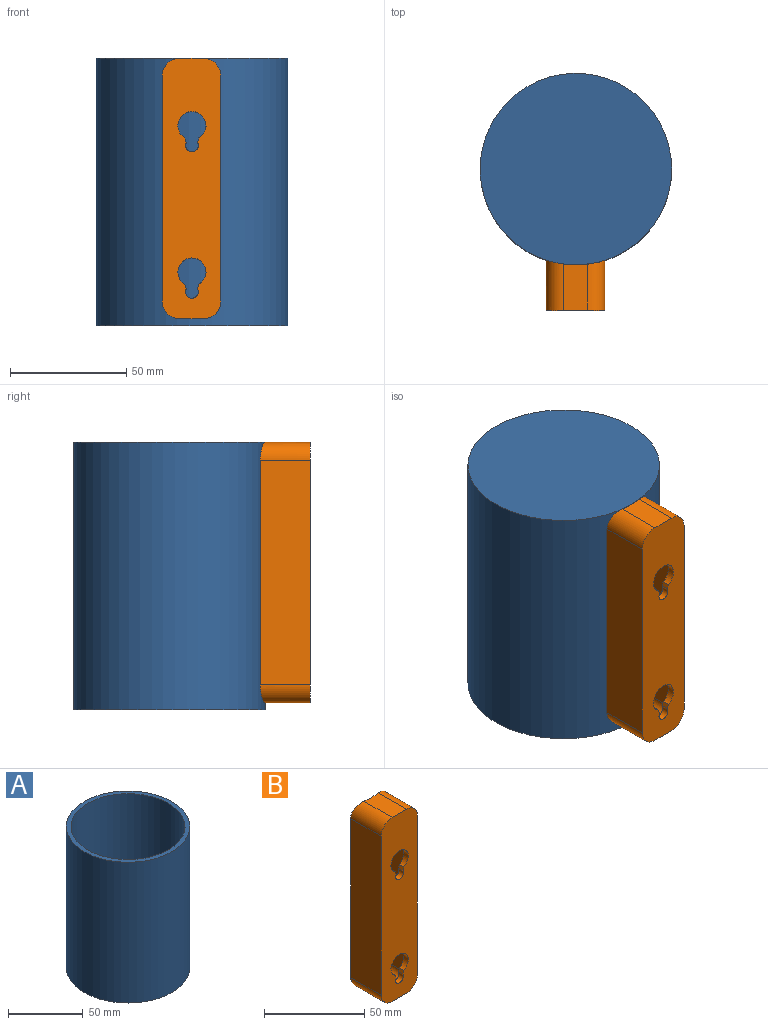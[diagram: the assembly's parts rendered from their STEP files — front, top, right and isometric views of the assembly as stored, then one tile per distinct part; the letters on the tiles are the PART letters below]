
ASSEMBLY  parts=2 mates=1
PART A: 5 faces, bbox 82.6x82.6x115.2 mm
  f0: plane 82.55x82.55mm, normal (0,0,1), area 791.7mm2, adj f1,f3
  f1: cylinder r=41.27mm len=115.17mm, axis (0,0,1), area 29868.7mm2, adj f0,f2
  f2: plane 82.55x82.55mm, normal (0,0,-1), area 5352.1mm2, adj f1
  f3: cylinder r=38.1mm len=112mm, axis (0,0,1), area 26811.1mm2, adj f0,f4
  f4: plane 76.2x76.2mm, normal (0,0,1), area 4560.4mm2, adj f3
PART B: 36 faces, bbox 25.4x21.6x112.2 mm
  f0: cylinder r=2.75mm len=5.49mm, axis (0,1,0), area 35.9mm2, adj f3,f5,f21,f31
  f1: cylinder r=6.08mm len=12.17mm, axis (0,1,0), area 101.4mm2, adj f2,f4,f20,f30
  f2: plane 3.18x1.97mm, normal (0.96,0,0.28), area 6.5mm2, adj f1,f16,f20,f30
  f3: plane 3.22x1.97mm, normal (0.96,0,0.28), area 6.5mm2, adj f0,f15,f21,f31
  f4: plane 3.18x1.97mm, normal (-0.96,0,0.28), area 6.5mm2, adj f1,f16,f20,f30
  f5: plane 3.22x1.97mm, normal (-0.96,0,0.28), area 6.5mm2, adj f0,f15,f21,f31
  f6: cylinder r=2.75mm len=5.49mm, axis (0,1,0), area 35.9mm2, adj f9,f11,f21,f31
  f7: cylinder r=6.08mm len=12.17mm, axis (0,1,0), area 101.4mm2, adj f8,f10,f20,f30
  f8: plane 3.18x1.97mm, normal (0.96,0,0.28), area 6.5mm2, adj f7,f13,f20,f30
  f9: plane 3.22x1.97mm, normal (0.96,0,0.28), area 6.5mm2, adj f6,f12,f21,f31
  f10: plane 3.18x1.97mm, normal (-0.96,0,0.28), area 6.5mm2, adj f7,f13,f20,f30
  f11: plane 3.22x1.97mm, normal (-0.96,0,0.28), area 6.5mm2, adj f6,f12,f21,f31
  f12: cylinder r=6.08mm len=12.17mm, axis (0,1,0), area 102mm2, adj f9,f11,f21,f31
  f13: cylinder r=2.75mm len=5.49mm, axis (0,1,0), area 35.8mm2, adj f8,f10,f20,f30
  f14: plane 96.93x21.48mm, normal (1,0,0), area 2081.7mm2, adj f20,f21,f23,f24
  f15: cylinder r=6.08mm len=12.17mm, axis (0,1,0), area 102mm2, adj f3,f5,f21,f31
  f16: cylinder r=2.75mm len=5.49mm, axis (0,1,0), area 35.8mm2, adj f2,f4,f20,f30
  f17: plane 96.93x21.59mm, normal (-1,0,0), area 2092.7mm2, adj f20,f21,f22,f25
  f18: plane 19.87x10.16mm, normal (0,0,-1), area 199.5mm2, adj f20,f21,f22,f23
  f19: plane 19.87x10.16mm, normal (0,0,1), area 199.5mm2, adj f20,f21,f24,f25
  f20: plane 112.17x25.4mm, normal (0,-1,0), area 2514.6mm2, adj f1,f2,f4,f7,f8,f10,f13,f14
  f21: cylinder r=41.27mm len=112.17mm, axis (0,0,-1), area 2559mm2, adj f0,f3,f5,f6,f9,f11,f12,f14
  f22: cylinder r=7.62mm len=21.59mm, axis (0,1,0), area 249.7mm2, adj f17,f18,f20,f21
  f23: cylinder r=7.62mm len=21.48mm, axis (0,-1,0), area 248.6mm2, adj f14,f18,f20,f21
  f24: cylinder r=7.62mm len=21.48mm, axis (0,1,0), area 248.6mm2, adj f14,f19,f20,f21
  f25: cylinder r=7.62mm len=21.59mm, axis (0,-1,0), area 249.7mm2, adj f17,f19,f20,f21
  f26: plane 96.93x14.18mm, normal (-1,0,0), area 1373.9mm2, adj f30,f31,f33,f34
  f27: plane 96.93x14.25mm, normal (1,0,0), area 1381.4mm2, adj f30,f31,f32,f35
  f28: plane 13.49x10.16mm, normal (0,0,1), area 134.9mm2, adj f30,f31,f32,f33
  f29: plane 13.49x10.16mm, normal (0,0,-1), area 134.9mm2, adj f30,f31,f34,f35
  f30: plane 105.82x19.05mm, normal (0,1,0), area 1714.2mm2, adj f1,f2,f4,f7,f8,f10,f13,f16
  f31: cylinder r=44.45mm len=105.82mm, axis (0,0,-1), area 1729.1mm2, adj f0,f3,f5,f6,f9,f11,f12,f15
  f32: cylinder r=4.45mm len=14.25mm, axis (0,1,0), area 97.4mm2, adj f27,f28,f30,f31
  f33: cylinder r=4.45mm len=14.18mm, axis (0,-1,0), area 96.9mm2, adj f26,f28,f30,f31
  f34: cylinder r=4.45mm len=14.18mm, axis (0,1,0), area 96.9mm2, adj f26,f29,f30,f31
  f35: cylinder r=4.45mm len=14.25mm, axis (0,-1,0), area 97.4mm2, adj f27,f29,f30,f31
PLACE A rot(axis=(1,0,0),180deg) t=(-46.6,-341.84,-36.56)mm
PLACE B t=(-46.6,-381.05,-69.28)mm
MATE fastened A.f1 <-> B.f21  axis (0,0,-1) through (-46.6,-341.84,30.24)mm
